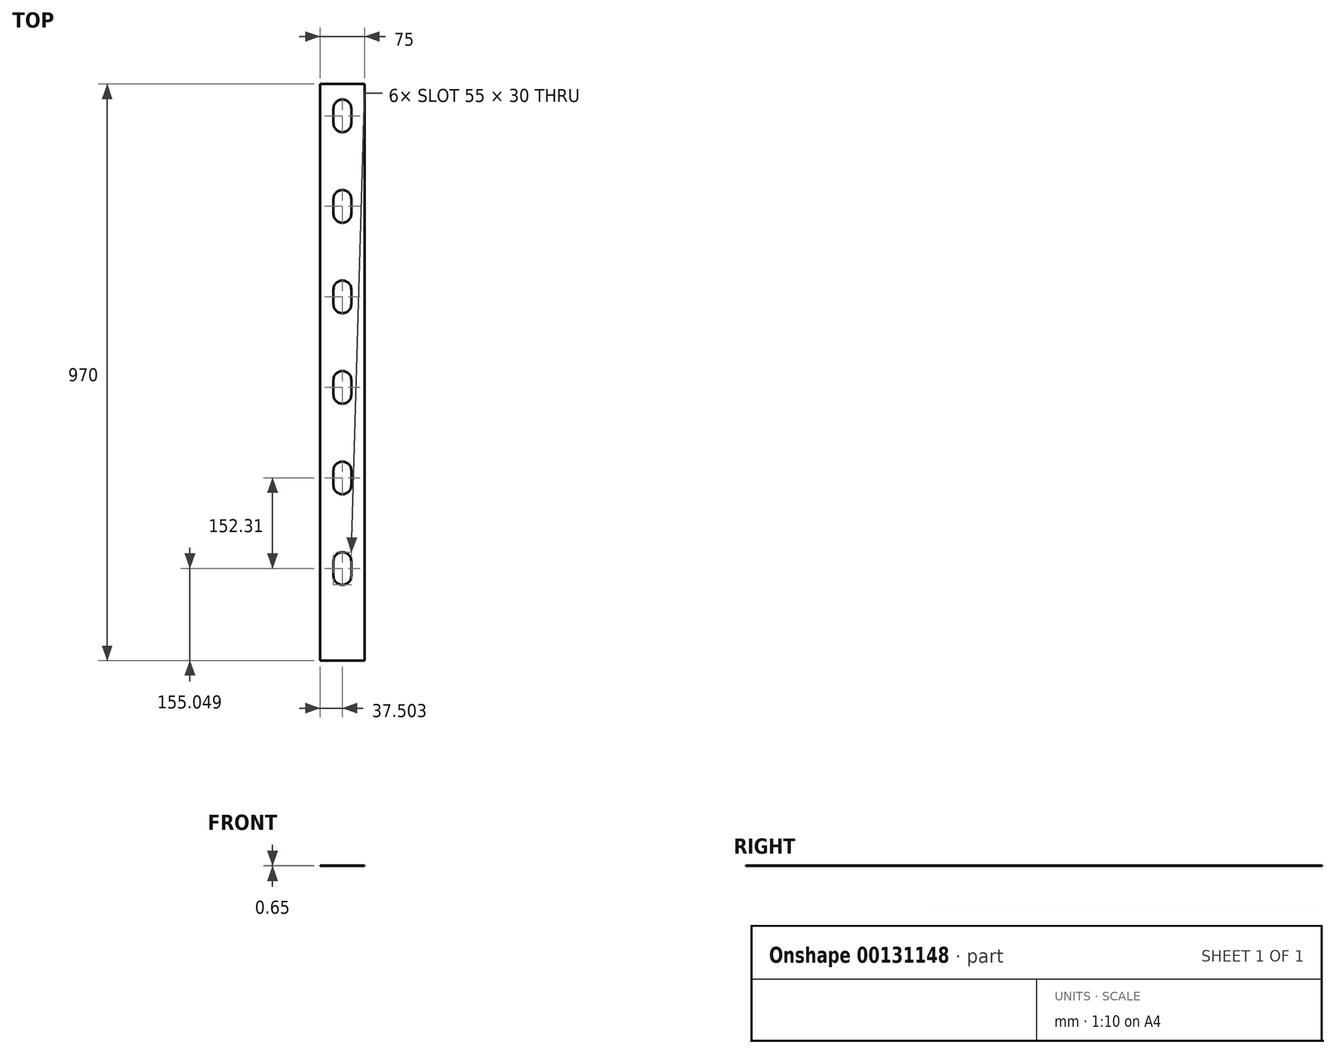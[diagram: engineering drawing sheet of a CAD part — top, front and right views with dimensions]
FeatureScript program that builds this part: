
annotation { "Feature Type Name" : "Feature", "Feature Type Description" : "" }
export const myFeature = defineFeature(function(context is Context, id is Id, definition is map)
    precondition{}
    {
        {
            var Q0;
            Q0=qCreatedBy(makeId("Top.planeOp"),FACE);
            var sketch = newSketch(context, id + "F0", { "sketchPlane" : qUnion([Q0])});
            skLineSegment(sketch, "E0.bottom", {"start": v(-88.8, -573.42) * mm, "end": v(-163.8, -573.42) * mm});
            skLineSegment(sketch, "E0.top", {"start": v(-88.8, 396.58) * mm, "end": v(-163.8, 396.58) * mm});
            skLineSegment(sketch, "E0.left", {"start": v(-88.8, -573.42) * mm, "end": v(-88.8, 396.58) * mm});
            skLineSegment(sketch, "E0.right", {"start": v(-163.8, -573.42) * mm, "end": v(-163.8, 396.58) * mm});
            skPoint(sketch, "E1.middle", {"position": v(148.88, -338.15) * mm});
            skArc(sketch, "E2", {"start": v(-141.3, -430.87) * mm, "mid": v(-126.3, -445.87) * mm, "end": v(-111.3, -430.87) * mm});
            skArc(sketch, "E3.trimOffspring", {"start": v(-111.3, -405.87) * mm, "mid": v(-126.3, -390.87) * mm, "end": v(-141.3, -405.87) * mm});
            skLineSegment(sketch, "E4", {"start": v(-141.3, -405.87) * mm, "end": v(-141.3, -430.87) * mm});
            skLineSegment(sketch, "E5", {"start": v(-111.3, -405.87) * mm, "end": v(-111.3, -430.87) * mm});
            skLineSegment(sketch, "E6", {"start": v(-126.3, -573.42) * mm, "end": v(-126.3, 396.58) * mm, "construction": true});
            skArc(sketch, "E7", {"start": v(-141.3, -126.25) * mm, "mid": v(-126.3, -141.25) * mm, "end": v(-111.3, -126.25) * mm});
            skArc(sketch, "E8.trimOffspring", {"start": v(-111.3, -101.25) * mm, "mid": v(-126.3, -86.25) * mm, "end": v(-141.3, -101.25) * mm});
            skLineSegment(sketch, "E9", {"start": v(-141.3, -101.25) * mm, "end": v(-141.3, -126.25) * mm});
            skLineSegment(sketch, "E10", {"start": v(-111.3, -101.25) * mm, "end": v(-111.3, -126.25) * mm});
            skArc(sketch, "E11", {"start": v(-141.3, -278.56) * mm, "mid": v(-126.3, -293.56) * mm, "end": v(-111.3, -278.56) * mm});
            skArc(sketch, "E12.trimOffspring", {"start": v(-111.3, -253.56) * mm, "mid": v(-126.3, -238.56) * mm, "end": v(-141.3, -253.56) * mm});
            skLineSegment(sketch, "E13", {"start": v(-141.3, -253.56) * mm, "end": v(-141.3, -278.56) * mm});
            skLineSegment(sketch, "E14", {"start": v(-111.3, -253.56) * mm, "end": v(-111.3, -278.56) * mm});
            skPoint(sketch, "E15.middle", {"position": v(216.86, -20.65) * mm});
            skArc(sketch, "E16", {"start": v(-141.3, 178.37) * mm, "mid": v(-126.3, 163.37) * mm, "end": v(-111.3, 178.37) * mm});
            skArc(sketch, "E17.trimOffspring", {"start": v(-111.3, 203.37) * mm, "mid": v(-126.3, 218.37) * mm, "end": v(-141.3, 203.37) * mm});
            skLineSegment(sketch, "E18", {"start": v(-141.3, 203.37) * mm, "end": v(-141.3, 178.37) * mm});
            skLineSegment(sketch, "E19", {"start": v(-111.3, 203.37) * mm, "end": v(-111.3, 178.37) * mm});
            skArc(sketch, "E20", {"start": v(-141.3, 26.06) * mm, "mid": v(-126.3, 11.06) * mm, "end": v(-111.3, 26.06) * mm});
            skArc(sketch, "E21.trimOffspring", {"start": v(-111.3, 51.06) * mm, "mid": v(-126.3, 66.06) * mm, "end": v(-141.3, 51.06) * mm});
            skLineSegment(sketch, "E22", {"start": v(-141.3, 51.06) * mm, "end": v(-141.3, 26.06) * mm});
            skLineSegment(sketch, "E23", {"start": v(-111.3, 51.06) * mm, "end": v(-111.3, 26.06) * mm});
            skPoint(sketch, "E24.middle", {"position": v(174.18, -74.29) * mm});
            skArc(sketch, "E25", {"start": v(-141.3, 330.68) * mm, "mid": v(-126.3, 315.68) * mm, "end": v(-111.3, 330.68) * mm});
            skArc(sketch, "E26.trimOffspring", {"start": v(-111.3, 355.68) * mm, "mid": v(-126.3, 370.68) * mm, "end": v(-141.3, 355.68) * mm});
            skLineSegment(sketch, "E27", {"start": v(-141.3, 355.68) * mm, "end": v(-141.3, 330.68) * mm});
            skLineSegment(sketch, "E28", {"start": v(-111.3, 355.68) * mm, "end": v(-111.3, 330.68) * mm});
            skSolve(sketch);
        }
        {
            var Q0;
            Q0=qSketchRegion(id+"F0",true);
            var Q1;
            Q1=makeQuery(id+"F0.imprint","IMPRINT",FACE,{"disambiguationData":[TD([[makeQuery(id+"F0.imprint","IMPRINT",EDGE,{"derivedFrom":sQuery(id+"F0.wireOp",EDGE,"E0.bottom")}),-1.0]])]});
            extrude(context, id + "F1", {"entities" : qUnion([Q0, Q1]), "depth" : 0.65 * mm});
        }
    });
